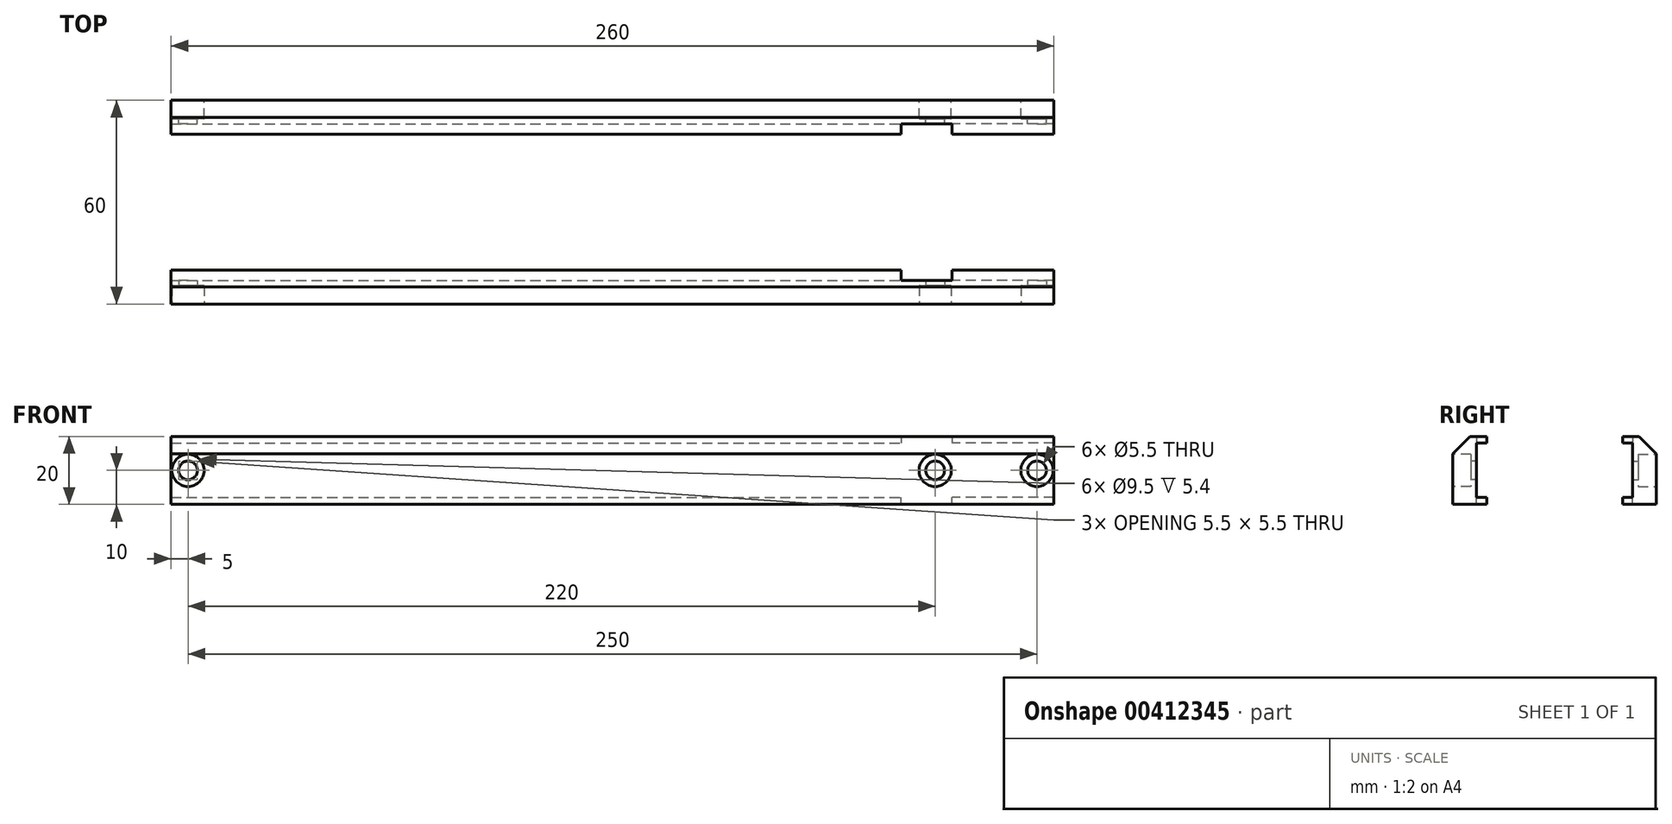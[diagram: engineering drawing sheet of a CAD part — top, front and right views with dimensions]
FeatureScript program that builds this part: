
annotation { "Feature Type Name" : "Feature", "Feature Type Description" : "" }
export const myFeature = defineFeature(function(context is Context, id is Id, definition is map)
    precondition{}
    {
        {
            var Q0;
            Q0=qCreatedBy(makeId("Front.planeOp"),FACE);
            var sketch = newSketch(context, id + "F0", { "sketchPlane" : qUnion([Q0])});
            skLineSegment(sketch, "E0.bottom", {"start": v(0, 0) * mm, "end": v(260, 0) * mm});
            skLineSegment(sketch, "E0.top", {"start": v(0, 20) * mm, "end": v(260, 20) * mm});
            skLineSegment(sketch, "E0.left", {"start": v(0, 0) * mm, "end": v(0, 20) * mm});
            skLineSegment(sketch, "E0.right", {"start": v(260, 0) * mm, "end": v(260, 20) * mm});
            skSolve(sketch);
        }
        {
            var Q0;
            Q0 = qSketchRegion(id + "F0", true);
            extrude(context, id + "F1", {"entities" : qUnion([Q0]), "depth" : 7 * mm});
        }
        {
            var Q0;
            Q0=makeQuery(id+"F1.opExtrude","CAP_FACE",FACE,{"disambiguationData":[OSD([sQuery(id+"F0.wireOp",EDGE,"E0.bottom"),sQuery(id+"F0.wireOp",EDGE,"E0.top"),sQuery(id+"F0.wireOp",EDGE,"E0.left"),sQuery(id+"F0.wireOp",EDGE,"E0.right")])],"isStart":true});
            var sketch = newSketch(context, id + "F2", { "sketchPlane" : qUnion([Q0])});
            skPoint(sketch, "E1", {"position": v(-5, 10) * mm});
            skPoint(sketch, "E2", {"position": v(-225, 10) * mm});
            skPoint(sketch, "E3", {"position": v(-255, 10) * mm});
            skSolve(sketch);
        }
        {
            var Q0;
            Q0=sQuery(id+"F2.wireOp",VERTEX,"E2");
            var Q1;
            Q1=sQuery(id+"F2.wireOp",VERTEX,"E1");
            var Q2;
            Q2=sQuery(id+"F2.wireOp",VERTEX,"E3");
            var Q3;
            Q3=makeQuery(id+"F1.opExtrude","SWEPT_BODY",BODY,{"disambiguationData":[OSD([sQuery(id+"F0.wireOp",EDGE,"E0.bottom"),sQuery(id+"F0.wireOp",EDGE,"E0.top"),sQuery(id+"F0.wireOp",EDGE,"E0.left"),sQuery(id+"F0.wireOp",EDGE,"E0.right")])]});
            hole(context, id + "F3", {"style" : HoleStyle.C_BORE, "endStyle" : HoleEndStyle.THROUGH, "holeDiameter" : 5.5 * mm, "cBoreDiameter" : 9.5 * mm, "cBoreDepth" : 5.4 * mm, "isTappedThrough" : true, "tappedDepth" : 2.6 * mm, "tapClearance" : 3, "locations" : qUnion([Q0, Q1, Q2]), "scope" : qUnion([Q3])});
        }
        {
            var Q0;
            Q0=makeQuery(id+"F1.opExtrude","CAP_FACE",FACE,{"disambiguationData":[OSD([sQuery(id+"F0.wireOp",EDGE,"E0.bottom"),sQuery(id+"F0.wireOp",EDGE,"E0.top"),sQuery(id+"F0.wireOp",EDGE,"E0.left"),sQuery(id+"F0.wireOp",EDGE,"E0.right")])],"isStart":false});
            var sketch = newSketch(context, id + "F4", { "sketchPlane" : qUnion([Q0])});
            skLineSegment(sketch, "E4.bottom", {"start": v(0, 20) * mm, "end": v(215, 20) * mm});
            skLineSegment(sketch, "E4.top", {"start": v(0, 18) * mm, "end": v(215, 18) * mm});
            skLineSegment(sketch, "E4.left", {"start": v(0, 20) * mm, "end": v(0, 18) * mm});
            skLineSegment(sketch, "E4.right", {"start": v(215, 20) * mm, "end": v(215, 18) * mm});
            skLineSegment(sketch, "E5.bottom", {"start": v(260, 20) * mm, "end": v(230, 20) * mm});
            skLineSegment(sketch, "E5.top", {"start": v(260, 18) * mm, "end": v(230, 18) * mm});
            skLineSegment(sketch, "E5.left", {"start": v(260, 20) * mm, "end": v(260, 18) * mm});
            skLineSegment(sketch, "E5.right", {"start": v(230, 20) * mm, "end": v(230, 18) * mm});
            skLineSegment(sketch, "E6.bottom", {"start": v(0, 0) * mm, "end": v(215, 0) * mm});
            skLineSegment(sketch, "E6.top", {"start": v(0, 2) * mm, "end": v(215, 2) * mm});
            skLineSegment(sketch, "E6.left", {"start": v(0, 0) * mm, "end": v(0, 2) * mm});
            skLineSegment(sketch, "E6.right", {"start": v(215, 0) * mm, "end": v(215, 2) * mm});
            skLineSegment(sketch, "E7.bottom", {"start": v(260, 0) * mm, "end": v(230, 0) * mm});
            skLineSegment(sketch, "E7.top", {"start": v(260, 2) * mm, "end": v(230, 2) * mm});
            skLineSegment(sketch, "E7.left", {"start": v(260, 0) * mm, "end": v(260, 2) * mm});
            skLineSegment(sketch, "E7.right", {"start": v(230, 0) * mm, "end": v(230, 2) * mm});
            skSolve(sketch);
        }
        {
            var Q0;
            Q0 = qSketchRegion(id + "F4", true);
            extrude(context, id + "F5", {"entities" : qUnion([Q0]), "operationType" : NewBodyOperationType.ADD, "depth" : 3 * mm});
        }
        {
            var Q0;
            Q0=makeQuery(id+"F1.opExtrude","CAP_EDGE",EDGE,{"disambiguationData":[OSD([sQuery(id+"F0.wireOp",EDGE,"E0.top")])],"isStart":true});
            chamfer(context, id + "F6", {"entities" : qUnion([Q0]), "width" : 5.08 * mm, "tangentPropagation" : true});
        }
        {
            var Q0;
            Q0=makeQuery(id+"F5.opExtrude","CAP_FACE",FACE,{"disambiguationData":[OSD([sQuery(id+"F4.wireOp",EDGE,"E4.bottom"),sQuery(id+"F4.wireOp",EDGE,"E4.top"),sQuery(id+"F4.wireOp",EDGE,"E4.left"),sQuery(id+"F4.wireOp",EDGE,"E4.right")])],"isStart":false});
            cPlane(context, id + "F7", {"entities" : qUnion([Q0]), "cplaneType" : CPlaneType.OFFSET, "offset" : 20 * mm, "width" : 152.4 * mm, "height" : 152.4 * mm});
        }
        {
            var Q0;
            Q0=makeQuery(id+"F1.opExtrude","SWEPT_BODY",BODY,{"disambiguationData":[OSD([sQuery(id+"F0.wireOp",EDGE,"E0.bottom"),sQuery(id+"F0.wireOp",EDGE,"E0.top"),sQuery(id+"F0.wireOp",EDGE,"E0.left"),sQuery(id+"F0.wireOp",EDGE,"E0.right")])]});
            var Q1;
            Q1=qCreatedBy(id+"F7.planeOp",FACE);
            mirror(context, id + "F8", {"entities" : qUnion([Q0]), "mirrorPlane" : qUnion([Q1])});
        }
    });
